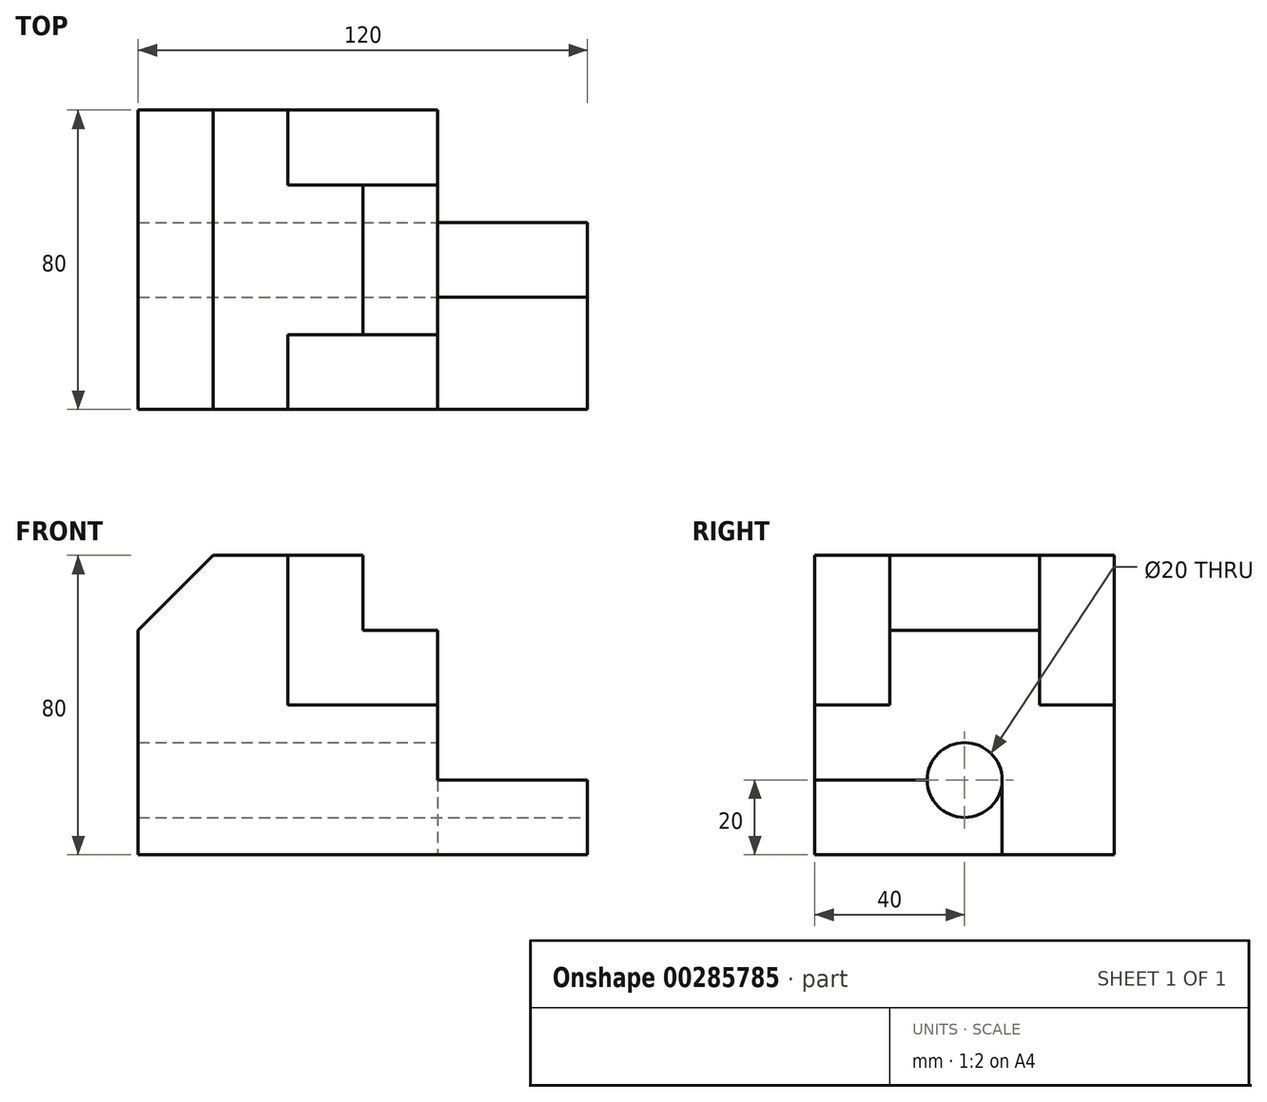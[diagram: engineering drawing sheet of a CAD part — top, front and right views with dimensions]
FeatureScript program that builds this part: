
annotation { "Feature Type Name" : "Feature", "Feature Type Description" : "" }
export const myFeature = defineFeature(function(context is Context, id is Id, definition is map)
    precondition{}
    {
        {
            var Q0;
            Q0=qCreatedBy(makeId("Top.planeOp"),FACE);
            var sketch = newSketch(context, id + "F0", { "sketchPlane" : qUnion([Q0])});
            skLineSegment(sketch, "E0.bottom", {"start": v(0, 0) * mm, "end": v(120, 0) * mm});
            skLineSegment(sketch, "E0.top", {"start": v(0, 80) * mm, "end": v(120, 80) * mm});
            skLineSegment(sketch, "E0.left", {"start": v(0, 0) * mm, "end": v(0, 80) * mm});
            skLineSegment(sketch, "E1", {"start": v(0, 80) * mm, "end": v(20, 80) * mm, "construction": true});
            skLineSegment(sketch, "E2", {"start": v(20, 80) * mm, "end": v(20, 0) * mm});
            skLineSegment(sketch, "E3", {"start": v(20, 80) * mm, "end": v(40, 80) * mm, "construction": true});
            skLineSegment(sketch, "E4", {"start": v(40, 80) * mm, "end": v(40, 60) * mm});
            skLineSegment(sketch, "E5", {"start": v(40, 60) * mm, "end": v(60, 60) * mm});
            skLineSegment(sketch, "E6", {"start": v(60, 60) * mm, "end": v(60, 20) * mm});
            skLineSegment(sketch, "E7", {"start": v(60, 20) * mm, "end": v(40, 20) * mm});
            skLineSegment(sketch, "E8", {"start": v(40, 20) * mm, "end": v(40, 0) * mm});
            skLineSegment(sketch, "E9", {"start": v(60, 60) * mm, "end": v(80, 60) * mm});
            skLineSegment(sketch, "E10", {"start": v(80, 60) * mm, "end": v(80, 20) * mm});
            skLineSegment(sketch, "E11", {"start": v(80, 20) * mm, "end": v(60, 20) * mm});
            skLineSegment(sketch, "E12", {"start": v(80, 60) * mm, "end": v(80, 80) * mm});
            skLineSegment(sketch, "E13", {"start": v(80, 80) * mm, "end": v(80, 0) * mm});
            skLineSegment(sketch, "E14", {"start": v(80, 60) * mm, "end": v(80, 50) * mm});
            skLineSegment(sketch, "E15", {"start": v(80, 50) * mm, "end": v(120, 50) * mm});
            skLineSegment(sketch, "E16", {"start": v(80, 50) * mm, "end": v(80, 30) * mm});
            skLineSegment(sketch, "E17", {"start": v(80, 30) * mm, "end": v(120, 30) * mm});
            skLineSegment(sketch, "E18", {"start": v(120, 80) * mm, "end": v(120, 0) * mm});
            skSolve(sketch);
        }
        {
            var Q0;
            {var subQ0=sQuery(id+"F0.wireOp",EDGE,"E0.left");Q0=makeQuery(id+"F0.imprint","IMPRINT",FACE,{"disambiguationData":[TD([[makeQuery(id+"F0.imprint","IMPRINT",EDGE,{"derivedFrom":subQ0}),-1.0]])]});}
            var Q1;
            {var subQ0=sQuery(id+"F0.wireOp",EDGE,"E2");Q1=makeQuery(id+"F0.imprint","IMPRINT",FACE,{"disambiguationData":[TD([[makeQuery(id+"F0.imprint","IMPRINT",EDGE,{"derivedFrom":subQ0}),1.0]])]});}
            extrude(context, id + "F1", {"entities" : qUnion([Q0, Q1]), "depth" : 80 * mm});
        }
        {
            var Q0;
            {var subQ0=sQuery(id+"F0.wireOp",EDGE,"E4");Q0=makeQuery(id+"F0.imprint","IMPRINT",FACE,{"disambiguationData":[TD([[makeQuery(id+"F0.imprint","IMPRINT",EDGE,{"derivedFrom":subQ0}),1.0]])]});}
            var Q1;
            Q1=makeQuery(id+"F0.imprint","IMPRINT",FACE,{"disambiguationData":[TD([[makeQuery(id+"F0.imprint","IMPRINT",EDGE,{"derivedFrom":sQuery(id+"F0.wireOp",EDGE,"E7")}),1.0]])]});
            extrude(context, id + "F2", {"entities" : qUnion([Q0, Q1]), "operationType" : NewBodyOperationType.ADD, "depth" : 40 * mm});
        }
        {
            var Q0;
            Q0=makeQuery(id+"F0.imprint","IMPRINT",FACE,{"disambiguationData":[TD([[makeQuery(id+"F0.imprint","IMPRINT",EDGE,{"derivedFrom":sQuery(id+"F0.wireOp",EDGE,"E6")}),1.0]])]});
            extrude(context, id + "F3", {"entities" : qUnion([Q0]), "operationType" : NewBodyOperationType.ADD, "depth" : 60 * mm});
        }
        {
            var Q0;
            {var subQ0=sQuery(id+"F0.wireOp",EDGE,"E0.bottom");Q0=makeQuery(id+"Fsqoz4LtmZ8sEMp_1.boolean.opBoolean","MERGE",FACE,{"derivedFrom":[makeQuery(id+"F2.boolean.opBoolean","MERGE",FACE,{"derivedFrom":[makeQuery(id+"F1.opExtrude","SWEPT_FACE",FACE,{"disambiguationData":[OSD([subQ0])]}),makeQuery(id+"F2.opExtrude","SWEPT_FACE",FACE,{"disambiguationData":[OSD([subQ0])]})]}),makeQuery(id+"Fsqoz4LtmZ8sEMp_1.opExtrude","SWEPT_FACE",FACE,{"disambiguationData":[OSD([sQuery(id+"F0.wireOp",EDGE,"urSJBMUE-N4N0-1PKx-Uujl-2Ylk5tS525Cj")])]})]});}
            var sketch = newSketch(context, id + "F4", { "sketchPlane" : qUnion([Q0])});
            skLineSegment(sketch, "E19", {"start": v(0, 80) * mm, "end": v(20, 80) * mm});
            skLineSegment(sketch, "E20", {"start": v(0, 80) * mm, "end": v(0, 60) * mm});
            skLineSegment(sketch, "E21", {"start": v(0, 60) * mm, "end": v(20, 80) * mm});
            skSolve(sketch);
        }
        {
            var Q0;
            Q0=makeQuery(id+"F4.imprint","IMPRINT",FACE,{"disambiguationData":[TD([[makeQuery(id+"F4.imprint","IMPRINT",EDGE,{"derivedFrom":sQuery(id+"F4.wireOp",EDGE,"E19")}),-1.0]])]});
            extrude(context, id + "F5", {"entities" : qUnion([Q0]), "operationType" : NewBodyOperationType.REMOVE, "oppositeDirection" : true, "depth" : 80 * mm});
        }
        {
            var Q0;
            {var subQ1=sQuery(id+"F0.wireOp",EDGE,"E14");Q0=makeQuery(id+"F0.imprint","IMPRINT",FACE,{"disambiguationData":[TD([[makeQuery(id+"F0.imprint","IMPRINT",EDGE,{"derivedFrom":subQ1}),1.0]])]});}
            var Q1;
            {var subQ4=sQuery(id+"F0.wireOp",EDGE,"E17");Q1=makeQuery(id+"F0.imprint","IMPRINT",FACE,{"disambiguationData":[TD([[makeQuery(id+"F0.imprint","IMPRINT",EDGE,{"derivedFrom":subQ4}),-1.0]])]});}
            var Q2;
            {var subQ0=sQuery(id+"F0.wireOp",EDGE,"E15");Q2=makeQuery(id+"F0.imprint","IMPRINT",FACE,{"disambiguationData":[TD([[makeQuery(id+"F0.imprint","IMPRINT",EDGE,{"derivedFrom":subQ0}),-1.0]])]});}
            extrude(context, id + "F6", {"entities" : qUnion([Q0, Q1, Q2]), "operationType" : NewBodyOperationType.ADD, "depth" : 20 * mm});
        }
        {
            var Q0;
            Q0=makeQuery(id+"F6.opExtrude","SWEPT_FACE",FACE,{"disambiguationData":[OSD([sQuery(id+"F0.wireOp",EDGE,"E18")])]});
            var sketch = newSketch(context, id + "F7", { "sketchPlane" : qUnion([Q0])});
            skCircle(sketch, "E22", {"center": v(40, 20) * mm, "radius": 10 * mm});
            skSolve(sketch);
        }
        {
            var Q0;
            Q0 = qSketchRegion(id + "F7", true);
            extrude(context, id + "F8", {"entities" : qUnion([Q0]), "operationType" : NewBodyOperationType.REMOVE, "oppositeDirection" : true, "depth" : 120 * mm});
        }
    });
